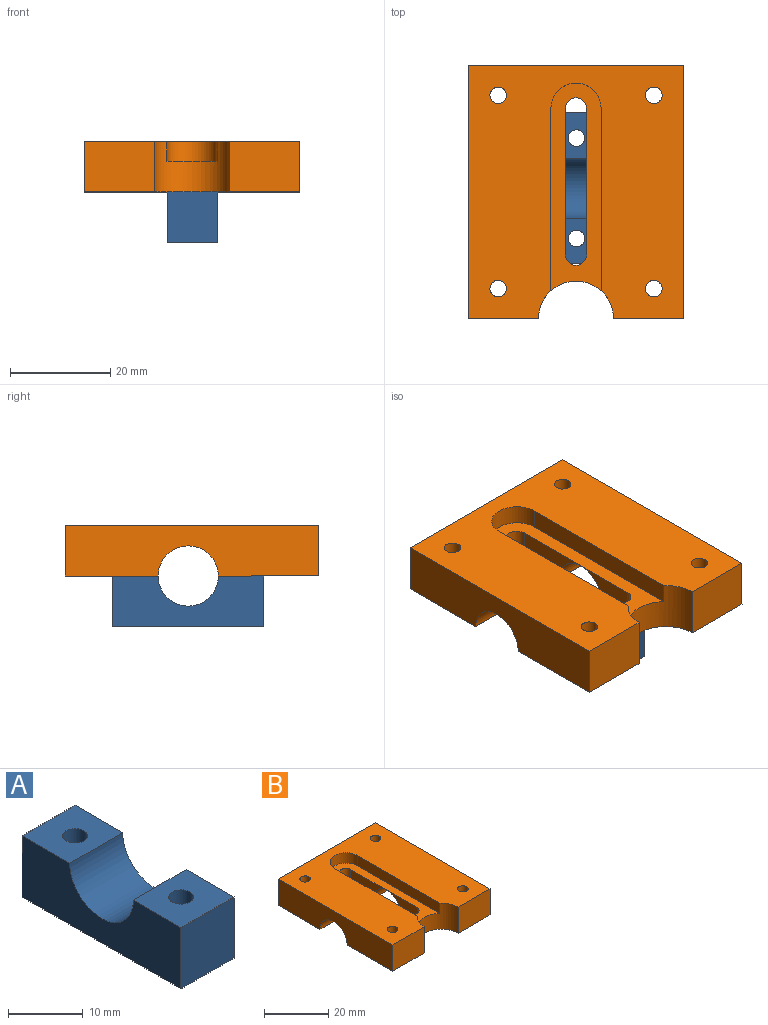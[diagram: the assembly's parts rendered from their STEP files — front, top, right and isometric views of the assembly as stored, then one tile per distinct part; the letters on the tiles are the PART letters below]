
ASSEMBLY  parts=2 mates=1
PART A: 10 faces, bbox 10x30x10 mm
  f0: plane 10x9mm, normal (0,0,1), area 81.4mm2, adj f1,f2,f4,f6,f9
  f1: plane 10x10mm, normal (0,-1,0), area 100mm2, adj f0,f2,f6,f8
  f2: plane 30x10mm, normal (1,0,0), area 243.5mm2, adj f0,f1,f3,f7,f8,f9
  f3: plane 10x10mm, normal (0,1,0), area 100mm2, adj f2,f6,f7,f8
  f4: cylinder r=1.65mm len=10mm, axis (0,0,-1), area 103.7mm2, adj f0,f8
  f5: cylinder r=1.65mm len=10mm, axis (0,0,-1), area 103.7mm2, adj f7,f8
  f6: plane 30x10mm, normal (-1,0,0), area 243.5mm2, adj f0,f1,f3,f7,f8,f9
  f7: plane 10x9mm, normal (0,0,1), area 81.4mm2, adj f2,f3,f5,f6,f9
  f8: plane 30x10mm, normal (0,0,-1), area 282.9mm2, adj f1,f2,f3,f4,f5,f6
  f9: cylinder r=6mm len=12mm, axis (-1,0,0), area 188.5mm2, adj f0,f2,f6,f7
PART B: 23 faces, bbox 43x50.5x10 mm
  f0: plane 43x20mm, normal (0,0,-1), area 717.2mm2, adj f3,f4,f5,f7,f8,f9,f11,f16
  f1: cylinder r=5mm len=10mm, axis (0,0,-1), area 61.3mm2, adj f2,f12,f14,f20
  f2: plane 36.34x3.9mm, normal (-1,0,0), area 141.7mm2, adj f1,f3,f14,f20
  f3: cylinder r=7.5mm len=15mm, axis (0,0,-1), area 192.9mm2, adj f0,f2,f4,f8,f12,f14,f20
  f4: plane 14x10mm, normal (0,-1,0), area 140mm2, adj f0,f3,f5,f14
  f5: plane 50.5x10mm, normal (1,0,0), area 448.5mm2, adj f0,f4,f6,f14,f15,f22
  f6: plane 43x10mm, normal (0,1,0), area 430mm2, adj f5,f7,f14,f15
  f7: plane 50.5x10mm, normal (-1,0,0), area 448.5mm2, adj f0,f6,f8,f14,f15,f21
  f8: plane 14x10mm, normal (0,-1,0), area 140mm2, adj f0,f3,f7,f14
  f9: cylinder r=1.65mm len=10mm, axis (0,0,-1), area 103.7mm2, adj f0,f14
  f10: cylinder r=1.65mm len=10mm, axis (0,0,-1), area 103.7mm2, adj f14,f15
  f11: cylinder r=1.65mm len=10mm, axis (0,0,-1), area 103.7mm2, adj f0,f14
  f12: plane 36.34x3.9mm, normal (1,0,0), area 141.7mm2, adj f1,f3,f14,f20
  f13: cylinder r=1.65mm len=10mm, axis (0,0,-1), area 103.7mm2, adj f14,f15
  f14: plane 50.5x43mm, normal (0,0,1), area 1659.4mm2, adj f1,f2,f3,f4,f5,f6,f7,f8
  f15: plane 43x18.5mm, normal (0,0,-1), area 729.8mm2, adj f5,f6,f7,f10,f13,f16,f18,f19
  f16: plane 29.18x6.1mm, normal (-1,0,0), area 121.4mm2, adj f0,f15,f17,f19,f20,f22
  f17: cylinder r=2.1mm len=6.1mm, axis (0,0,-1), area 40.2mm2, adj f0,f16,f18,f20
  f18: plane 29.18x6.1mm, normal (1,0,0), area 121.4mm2, adj f0,f15,f17,f19,f20,f21
  f19: cylinder r=2.1mm len=6.1mm, axis (0,0,-1), area 40.2mm2, adj f15,f16,f18,f20
  f20: plane 41.34x10mm, normal (0,0,1), area 253.1mm2, adj f1,f2,f3,f12,f16,f17,f18,f19
  f21: cylinder r=6mm len=19.4mm, axis (-1,0,0), area 365.7mm2, adj f0,f7,f15,f18
  f22: cylinder r=6mm len=19.4mm, axis (-1,0,0), area 365.7mm2, adj f0,f5,f15,f16
PLACE A rot(axis=(-0.97,-0.23,-0.02),0deg) t=(43.72,-31.55,10.37)mm
PLACE B rot(axis=(-0.97,-0.23,-0.02),0deg) t=(65.12,-47.55,20.37)mm
MATE fastened B.f21 <-> A.f9  axis (-1,0,0) through (45.72,-21.55,20.37)mm
